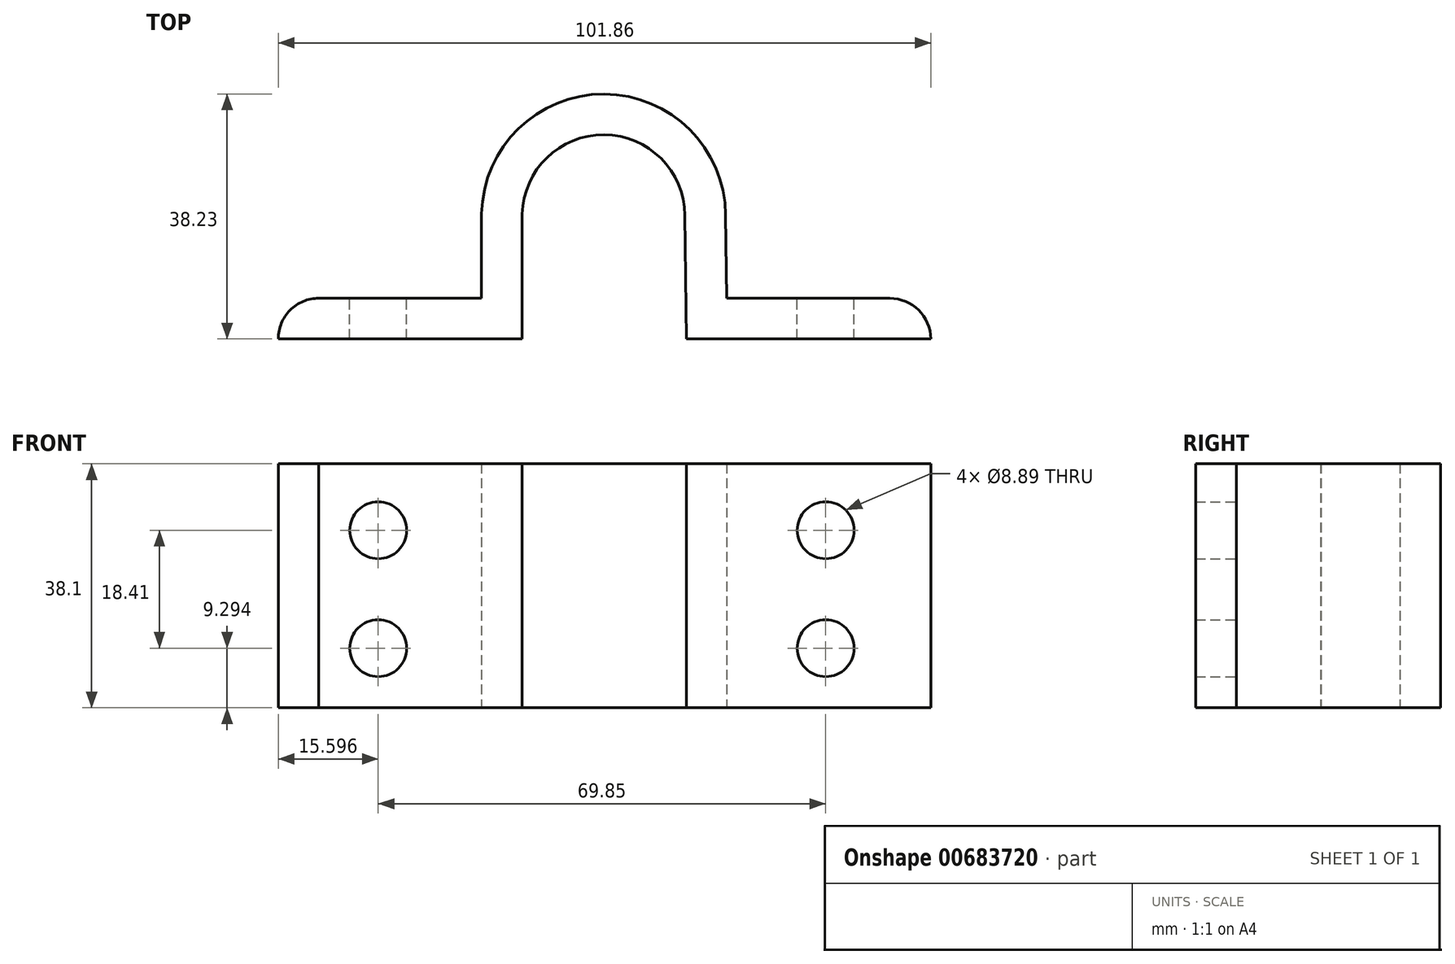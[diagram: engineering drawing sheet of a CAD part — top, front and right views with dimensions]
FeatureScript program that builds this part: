
annotation { "Feature Type Name" : "Feature", "Feature Type Description" : "" }
export const myFeature = defineFeature(function(context is Context, id is Id, definition is map)
    precondition{}
    {
        {
            var Q0;
            Q0=qCreatedBy(makeId("Top.planeOp"),FACE);
            var sketch = newSketch(context, id + "F0", { "sketchPlane" : qUnion([Q0])});
            skLineSegment(sketch, "E0", {"start": v(-44.5, 0) * mm, "end": v(44.58, 0) * mm, "construction": true});
            skLineSegment(sketch, "E1", {"start": v(-44.5, 31.88) * mm, "end": v(54.46, 31.88) * mm, "construction": true});
            skLineSegment(sketch, "E2", {"start": v(0, 0) * mm, "end": v(0, 31.88) * mm, "construction": true});
            skArc(sketch, "E3", {"start": v(12.64, 19.3) * mm, "mid": v(8.9, 28.18) * mm, "end": v(0, 31.88) * mm});
            skArc(sketch, "E4", {"start": v(0, 31.88) * mm, "mid": v(-8.92, 28.28) * mm, "end": v(-12.76, 19.47) * mm});
            skLineSegment(sketch, "E5", {"start": v(-12.76, 19.47) * mm, "end": v(-12.76, 0) * mm});
            skLineSegment(sketch, "E6", {"start": v(12.64, 19.3) * mm, "end": v(12.83, 0) * mm});
            skLineSegment(sketch, "E7", {"start": v(12.83, 0) * mm, "end": v(44.58, 0) * mm});
            skLineSegment(sketch, "E8", {"start": v(-12.76, 0) * mm, "end": v(-44.5, 0) * mm});
            skLineSegment(sketch, "E9.0", {"start": v(19.12, 6.35) * mm, "end": v(44.58, 6.35) * mm});
            skLineSegment(sketch, "E9.1", {"start": v(18.99, 19.37) * mm, "end": v(19.12, 6.35) * mm});
            skArc(sketch, "E9.2", {"start": v(18.99, 19.37) * mm, "mid": v(13.37, 32.68) * mm, "end": v(0.03, 38.23) * mm});
            skArc(sketch, "E9.3", {"start": v(0.03, 38.23) * mm, "mid": v(-13.37, 32.8) * mm, "end": v(-19.1, 19.53) * mm});
            skLineSegment(sketch, "E9.4", {"start": v(-19.1, 19.53) * mm, "end": v(-19.1, 6.35) * mm});
            skLineSegment(sketch, "E9.5", {"start": v(-19.1, 6.35) * mm, "end": v(-44.5, 6.35) * mm});
            skLineSegment(sketch, "E10", {"start": v(-44.5, 0) * mm, "end": v(-44.5, 0.02) * mm});
            skArc(sketch, "E11", {"start": v(-44.5, 6.35) * mm, "mid": v(-49, 4.49) * mm, "end": v(-50.84, 0) * mm});
            skArc(sketch, "E12", {"start": v(44.58, 6.35) * mm, "mid": v(49.1, 4.5) * mm, "end": v(51.02, 0) * mm});
            skLineSegment(sketch, "E13", {"start": v(44.58, 0) * mm, "end": v(51.02, 0) * mm});
            skLineSegment(sketch, "E14", {"start": v(-44.5, 0.02) * mm, "end": v(-50.84, 0) * mm});
            skSolve(sketch);
        }
        {
            var Q0;
            Q0=makeQuery(id+"F0.imprint","IMPRINT",FACE,{"disambiguationData":[TD([[makeQuery(id+"F0.imprint","IMPRINT",EDGE,{"derivedFrom":sQuery(id+"F0.wireOp",EDGE,"E3")}),-1.0]])]});
            extrude(context, id + "F1", {"entities" : qUnion([Q0]), "flatOperationType" : FlatOperationType.REMOVE, "offsetDistance" : 25 * mm, "depth" : 38.1 * mm, "domain" : OperationDomain.MODEL});
        }
        {
            var Q0;
            Q0=makeQuery(id+"F1.opExtrude","SWEPT_FACE",FACE,{"disambiguationData":[OSD([sQuery(id+"F0.wireOp",EDGE,"E9.0")])]});
            var sketch = newSketch(context, id + "F2", { "sketchPlane" : qUnion([Q0])});
            skCircle(sketch, "E15", {"center": v(-34.6, 27.7) * mm, "radius": 4.45 * mm});
            skCircle(sketch, "E16.0.1.0", {"center": v(-34.6, 9.3) * mm, "radius": 4.45 * mm});
            skCircle(sketch, "E16.1.0.0", {"center": v(35.24, 27.7) * mm, "radius": 4.45 * mm});
            skCircle(sketch, "E16.1.1.0", {"center": v(35.24, 9.3) * mm, "radius": 4.45 * mm});
            skLineSegment(sketch, "E16.direction1", {"start": v(-34.6, 27.7) * mm, "end": v(35.24, 27.7) * mm, "construction": true});
            skLineSegment(sketch, "E16.direction2", {"start": v(-34.6, 27.7) * mm, "end": v(-34.6, 9.3) * mm, "construction": true});
            skSolve(sketch);
        }
        {
            var Q0;
            Q0=qSketchRegion(id+"F2",true);
            extrude(context, id + "F3", {"entities" : qUnion([Q0]), "operationType" : NewBodyOperationType.REMOVE, "endBound" : BoundingType.THROUGH_ALL, "oppositeDirection" : true, "depth" : 25.4 * mm});
        }
    });
